# Revit family: RBA4007-212
name_source: partatom
category: Plumbing Fixtures
units: mm (PartAtom-declared; Revit-internal decimal feet)

## family parameters
Always vertical = Yes
Cut with Voids When Loaded = No
Part Type = Normal
Room Calculation Point = No
Round Connector Dimension = Use Diameter
Shared = Yes
Work Plane-Based = No

## types (1)
- RBA4007-212
    Bar & Fixing Plate = Stainless Steel - Type 304 - Satin Finish
    Default Elevation = 0 mm  [stored 0 ft]
    Description = Drop Down Rail for Bariatric, Left Hand
    Diameter = 32 mm  [stored 0.104987 ft]
    Footing = Plastic, Opaque Black
    Manufacturer = RBA Group
    Materials and Finishes = Gloss White Powder Coat
    Model = RBA4007-112
    Modified Issue = 20220714.01
    URL = http://www.rba.com.au

note: [stored X ft] marks values corroborated as IEEE doubles in the binary element streams (Revit-internal decimal feet)

## geometry (parser evidence)
native form markers: Blend x8, Sweep x3
no freeform markers — native parametric forms only
